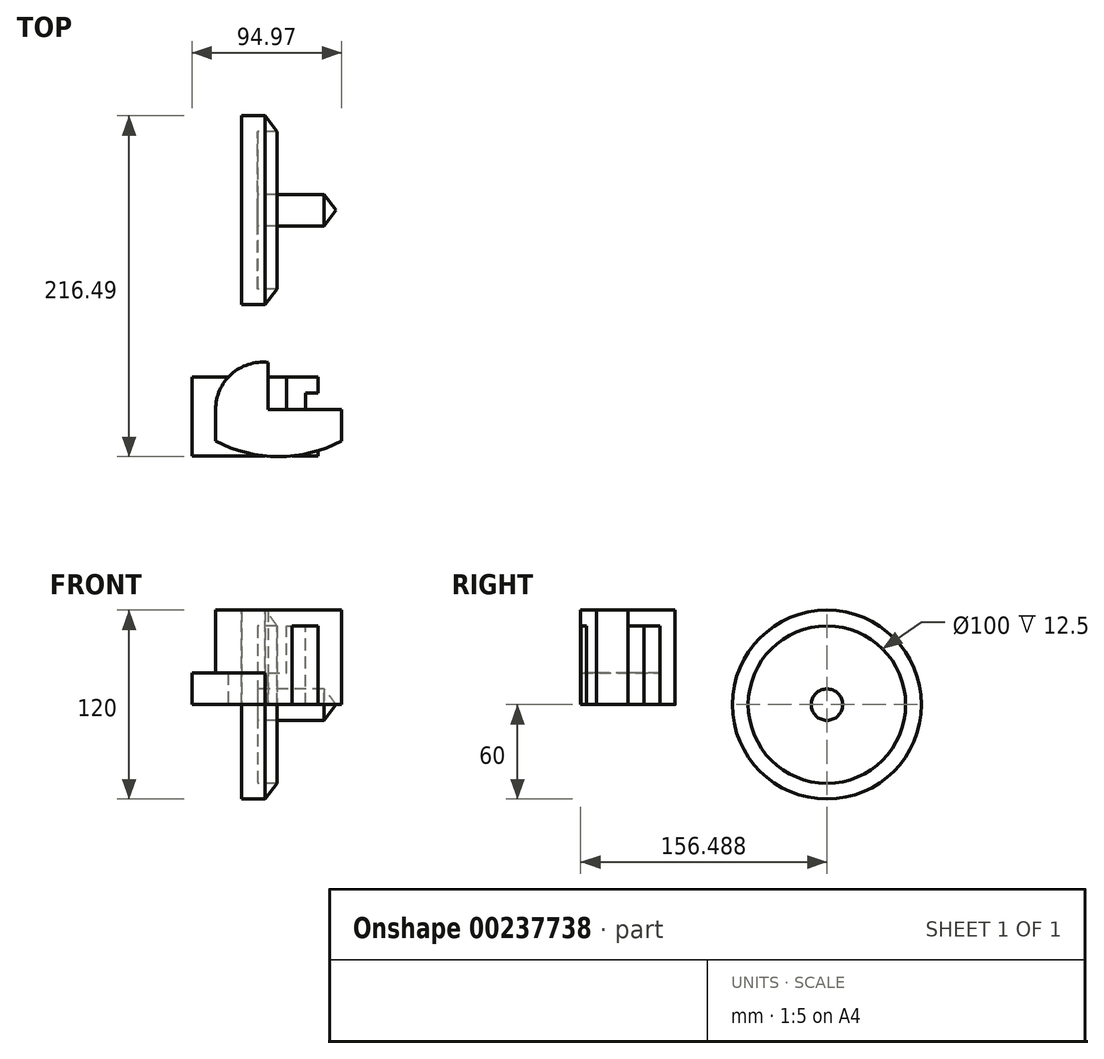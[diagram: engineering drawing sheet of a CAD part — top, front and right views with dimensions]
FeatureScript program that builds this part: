
annotation { "Feature Type Name" : "Feature", "Feature Type Description" : "" }
export const myFeature = defineFeature(function(context is Context, id is Id, definition is map)
    precondition{}
    {
        {
            var Q0;
            Q0=qCreatedBy(makeId("Top.planeOp"),FACE);
            var sketch = newSketch(context, id + "F0", { "sketchPlane" : qUnion([Q0])});
            skLineSegment(sketch, "E0", {"start": v(-48.54, 147.35) * mm, "end": v(-48.54, 87.35) * mm});
            skLineSegment(sketch, "E1", {"start": v(-48.54, 87.35) * mm, "end": v(11.46, 87.35) * mm});
            skLineSegment(sketch, "E2", {"start": v(-33.54, 147.35) * mm, "end": v(-48.54, 147.35) * mm});
            skLineSegment(sketch, "E3", {"start": v(-38.54, 97.35) * mm, "end": v(3.96, 97.35) * mm});
            skLineSegment(sketch, "E4", {"start": v(-38.54, 97.35) * mm, "end": v(-38.54, 137.35) * mm});
            skLineSegment(sketch, "E5", {"start": v(-38.54, 137.35) * mm, "end": v(-26.04, 137.35) * mm});
            skLineSegment(sketch, "E6", {"start": v(-33.54, 147.35) * mm, "end": v(-26.04, 137.35) * mm});
            skLineSegment(sketch, "E7", {"start": v(3.96, 97.35) * mm, "end": v(11.46, 87.35) * mm});
            skSolve(sketch);
        }
        {
            var Q0;
            Q0=qCreatedBy(makeId("Top.planeOp"),FACE);
            var sketch = newSketch(context, id + "F1", { "sketchPlane" : qUnion([Q0])});
            skLineSegment(sketch, "E8", {"start": v(-31.85, -9.3) * mm, "end": v(-31.85, -39.14) * mm});
            skLineSegment(sketch, "E9", {"start": v(-31.85, -39.14) * mm, "end": v(14.95, -39.14) * mm});
            skLineSegment(sketch, "E10", {"start": v(14.95, -39.14) * mm, "end": v(14.95, -59.14) * mm});
            skArc(sketch, "E11", {"start": v(-65.05, -59.14) * mm, "mid": v(-25.05, -69.14) * mm, "end": v(14.95, -59.14) * mm});
            skArc(sketch, "E12", {"start": v(-31.85, -9.3) * mm, "mid": v(-55.1, -16.82) * mm, "end": v(-65.05, -39.14) * mm});
            skLineSegment(sketch, "E13", {"start": v(-65.05, -39.14) * mm, "end": v(-65.05, -59.14) * mm});
            skSolve(sketch);
        }
        {
            var Q0;
            Q0 = qSketchRegion(id + "F1", true);
            extrude(context, id + "F2", {"entities" : qUnion([Q0]), "depth" : 60 * mm});
        }
        {
            var Q0;
            Q0=makeQuery(id+"F0.imprint","IMPRINT",FACE,{"disambiguationData":[TD([[makeQuery(id+"F0.imprint","IMPRINT",EDGE,{"derivedFrom":sQuery(id+"F0.wireOp",EDGE,"E0")}),1.0]])]});
            var Q1;
            Q1=sQuery(id+"F0.wireOp",EDGE,"E1");
            revolve(context, id + "F3", {"operationType" : NewBodyOperationType.ADD, "entities" : qUnion([Q0]), "axis" : qUnion([Q1]), "revolveType" : RevolveType.FULL});
        }
        {
            var Q0;
            Q0=qCreatedBy(makeId("Top.planeOp"),FACE);
            var sketch = newSketch(context, id + "F4", { "sketchPlane" : qUnion([Q0])});
            skLineSegment(sketch, "E14.bottom", {"start": v(-80.02, -68.71) * mm, "end": v(-20.02, -68.71) * mm});
            skLineSegment(sketch, "E14.top", {"start": v(-80.02, -18.71) * mm, "end": v(-20.02, -18.71) * mm});
            skLineSegment(sketch, "E14.left", {"start": v(-80.02, -68.71) * mm, "end": v(-80.02, -18.71) * mm});
            skLineSegment(sketch, "E14.right", {"start": v(-20.02, -68.71) * mm, "end": v(-20.02, -18.71) * mm});
            skLineSegment(sketch, "E15.bottom", {"start": v(-20.02, -18.71) * mm, "end": v(-0.02, -18.71) * mm});
            skLineSegment(sketch, "E15.top", {"start": v(-20.02, -68.71) * mm, "end": v(-0.02, -68.71) * mm});
            skLineSegment(sketch, "E15.left", {"start": v(-20.02, -18.71) * mm, "end": v(-20.02, -68.71) * mm});
            skLineSegment(sketch, "E15.right", {"start": v(-0.02, -18.71) * mm, "end": v(-0.02, -68.71) * mm});
            skLineSegment(sketch, "E16.bottom", {"start": v(-0.02, -58.71) * mm, "end": v(-8.02, -58.71) * mm});
            skLineSegment(sketch, "E16.top", {"start": v(-0.02, -28.71) * mm, "end": v(-8.02, -28.71) * mm});
            skLineSegment(sketch, "E16.left", {"start": v(-0.02, -58.71) * mm, "end": v(-0.02, -28.71) * mm});
            skLineSegment(sketch, "E16.right", {"start": v(-8.02, -58.71) * mm, "end": v(-8.02, -28.71) * mm});
            skSolve(sketch);
        }
        {
            var Q0;
            {var subQ1=sQuery(id+"F4.wireOp",EDGE,"E15.bottom");Q0=makeQuery(id+"F4.imprint","IMPRINT",FACE,{"disambiguationData":[TD([[makeQuery(id+"F4.imprint","IMPRINT",EDGE,{"derivedFrom":subQ1}),-1.0]])]});}
            extrude(context, id + "F5", {"entities" : qUnion([Q0]), "depth" : 50 * mm});
        }
        {
            var Q0;
            Q0=makeQuery(id+"F4.imprint","IMPRINT",FACE,{"disambiguationData":[TD([[makeQuery(id+"F4.imprint","IMPRINT",EDGE,{"derivedFrom":sQuery(id+"F4.wireOp",EDGE,"E14.bottom")}),1.0]])]});
            extrude(context, id + "F6", {"entities" : qUnion([Q0]), "operationType" : NewBodyOperationType.ADD, "depth" : 20 * mm});
        }
    });
